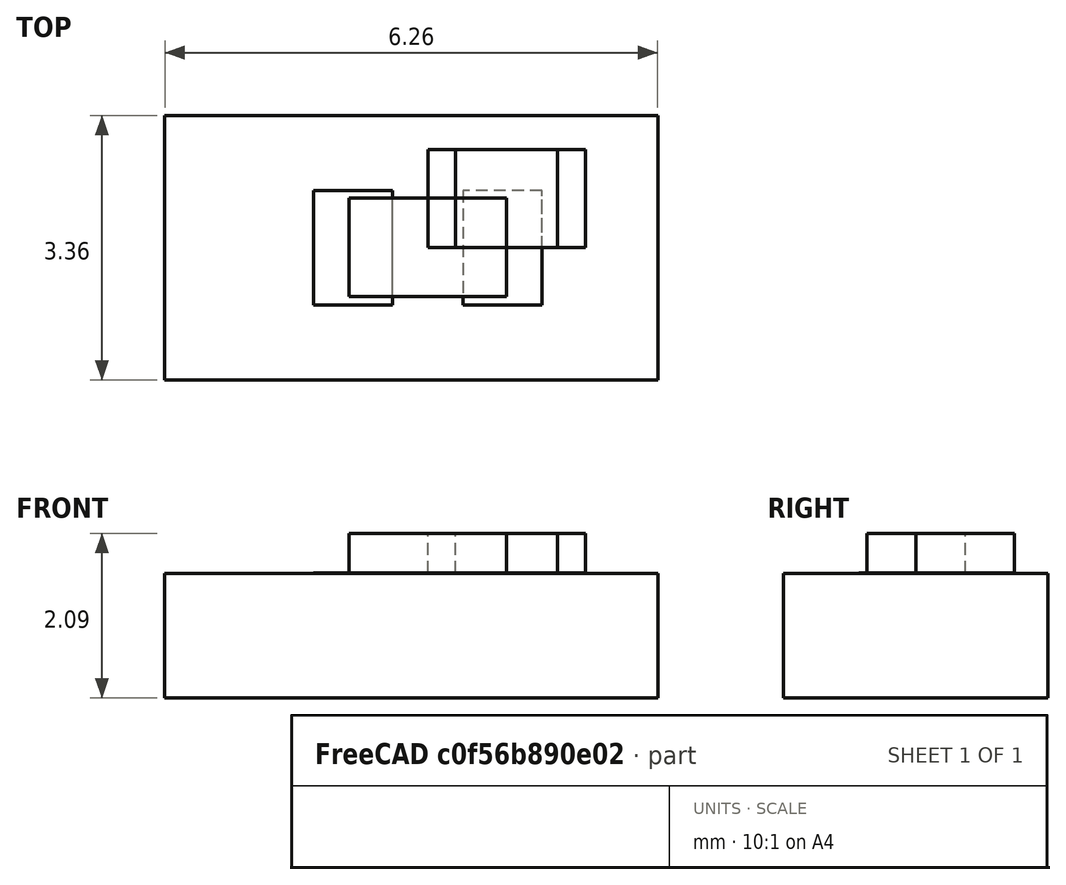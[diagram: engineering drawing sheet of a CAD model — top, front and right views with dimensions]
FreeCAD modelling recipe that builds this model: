
FCSTD DOCUMENT  (FreeCAD 0.17R13541 (Git))
Label: CAPCP2012X100N
License: All rights reserved
LicenseURL: http://en.wikipedia.org/wiki/All_rights_reserved
objects: Part::FeaturePython×4, Part::Box×3, App::DocumentObjectGroup×1, Part::Feature×1
note: 8 computed .brp shape members not serialized (recipe doc carries the construction recipe); baked Part::Feature solids carry a one-line shape summary decoded from their .brp

FEATURE [Part::Box] Box  label="pad1"
  AttacherType = Attacher::AttachEngine3D
  Height = 0.5
  Length = 0.35
  Width = 1.25
FEATURE [Part::Box] Box001  label="body"
  AttacherType = Attacher::AttachEngine3D
  Height = 0.5
  Length = 1.3
  Placement = pos=(0.35,0,0) rot=(0,0,1;0rad)
  Width = 1.25
  expr: Length = 2 - 0.34999999999999998 - 0.34999999999999998
FEATURE [Part::Box] Box002  label="pad2"
  AttacherType = Attacher::AttachEngine3D
  Height = 0.5
  Length = 0.35
  Placement = pos=(1.65,0,0) rot=(0,0,1;0rad)
  Width = 1.25
  expr: Placement.Base.x = 2 - 0.34999999999999998
FEATURE [Part::FeaturePython] FCrtYd_lines  label="FCrtYd"  # a2plus imported part (geometry in sourceFile) (typed FeaturePython)
  fixedPosition = true
FEATURE [Part::FeaturePython] Filk_lines  label="FrontSilk"  # a2plus imported part (geometry in sourceFile) (typed FeaturePython)
  fixedPosition = true
FEATURE [Part::FeaturePython] TopPads  # a2plus imported part (geometry in sourceFile) (typed FeaturePython)
  fixedPosition = true
FEATURE [Part::FeaturePython] newPCB  label="Pcb"  # a2plus imported part (geometry in sourceFile) (typed FeaturePython)
  fixedPosition = true
FEATURE [App::DocumentObjectGroup] CAPCP2012X100N_fp
  Group = -> [FCrtYd_lines,Filk_lines,TopPads,newPCB]
FEATURE [Part::Feature] Shape001  label="CAPCP2012X100N"
  shape: bbox 2 x 1.25 x 0.5 mm, 14 faces (baked)
